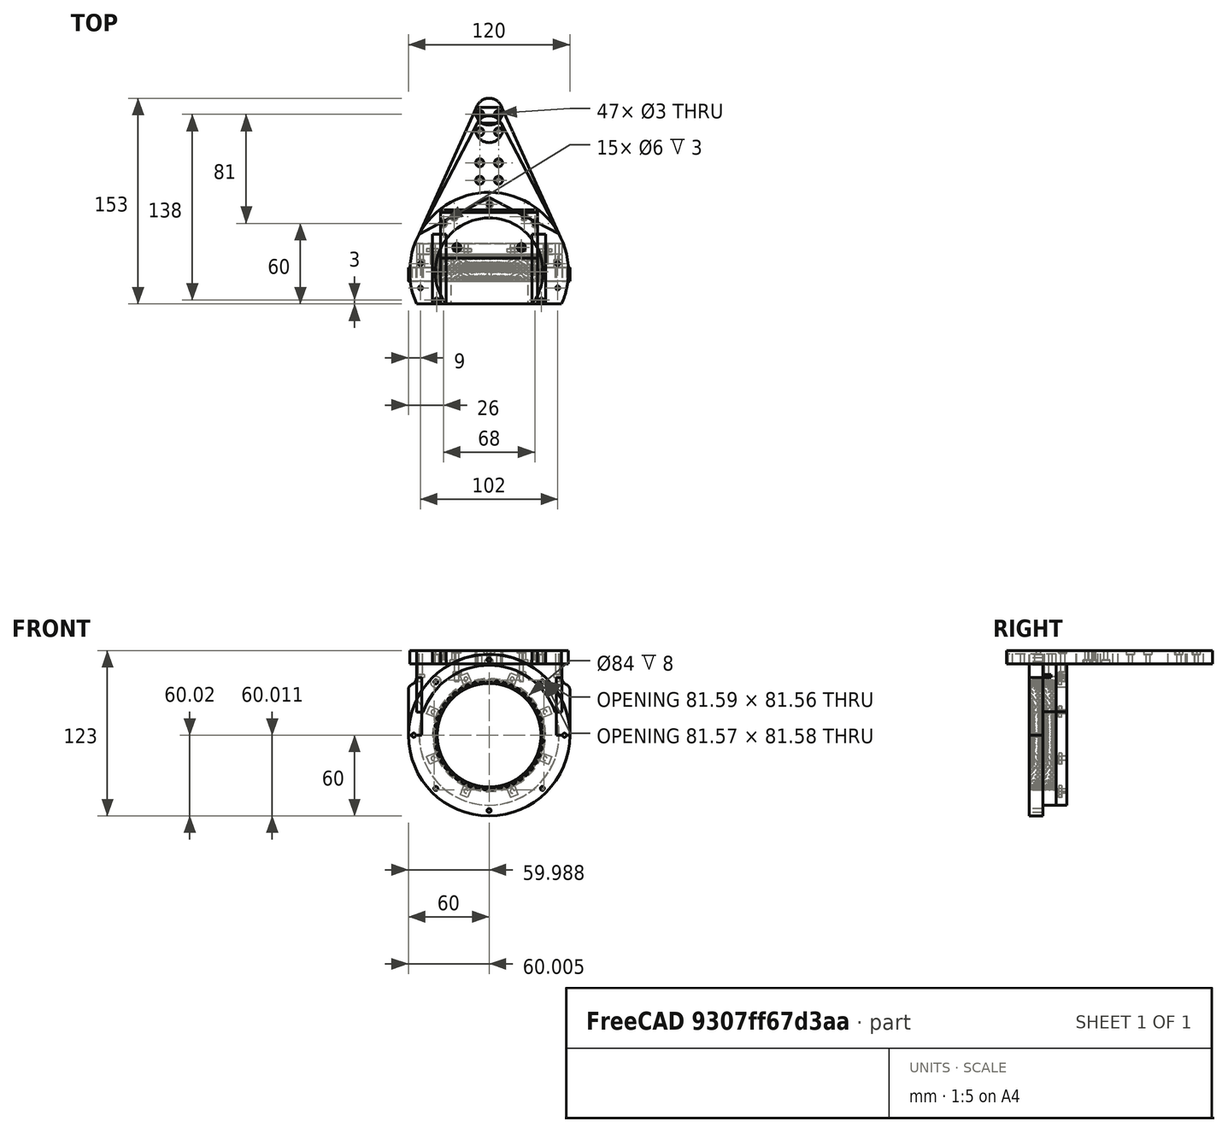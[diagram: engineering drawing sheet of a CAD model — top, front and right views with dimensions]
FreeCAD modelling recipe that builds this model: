
FCSTD DOCUMENT  (FreeCAD 0.19R24276 (Git))
Label: bazovina-part-A_trojuhelnikovina_012
License: All rights reserved
LicenseURL: http://en.wikipedia.org/wiki/All_rights_reserved
objects: Part::Cylinder×172, Part::Compound×74, Part::Cut×62, Part::Box×39, Part::FeaturePython×5, Part::Fillet×3, Sketcher::SketchObject×2, PartDesign::Pad×2, PartDesign::Body×2, Mesh::Feature×1
note: 363 computed .brp shape members not serialized (recipe doc carries the construction recipe); baked Part::Feature solids carry a one-line shape summary decoded from their .brp

FEATURE [Part::Cylinder] Cylinder284  label="Válec284"
  Angle = 360
  AttacherType = Attacher::AttachEngine3D
  Height = 10
  Placement = pos=(0,106,0) rot=(0,0,1;0rad)
  Radius = 10
FEATURE [Part::Box] Box135  label="Krychle135"
  AttacherType = Attacher::AttachEngine3D
  Height = 32
  Length = 200
  Placement = pos=(-100,-124,0) rot=(0,0,1;0rad)
  Width = 100
FEATURE [Part::Box] Box136  label="Krychle136"
  AttacherType = Attacher::AttachEngine3D
  Height = 10
  Length = 10
  Placement = pos=(32,-24,0) rot=(0,0,1;0rad)
  Width = 52
FEATURE [Part::FeaturePython] Tube  # WARN: FeaturePython — macro-defined, semantics opaque (R4)
  AttacherType = Attacher::AttachEngine3D
  Height = 10
  InnerRadius = 40
  OuterRadius = 59
FEATURE [Part::Cylinder] Cylinder292  label="Válec292"
  Angle = 360
  AttacherType = Attacher::AttachEngine3D
  Height = 100
  Placement = pos=(51,-12,0) rot=(0,0,1;0rad)
  Radius = 1.5
FEATURE [Part::Cylinder] Cylinder312  label="Válec312"
  Angle = 360
  AttacherType = Attacher::AttachEngine3D
  Height = 4
  Placement = pos=(34,36,-1) rot=(0,0,1;0rad)
  Radius = 3
FEATURE [Part::Cylinder] Cylinder311  label="Válec311"
  Angle = 360
  AttacherType = Attacher::AttachEngine3D
  Height = 4
  Placement = pos=(-34,36,-1) rot=(0,0,1;0rad)
  Radius = 3
FEATURE [Part::Compound] Compound290
  Links = -> [Cylinder312,Cylinder311]
FEATURE [Part::Cut] Cut136
  Base = -> Tube
  Tool = -> Compound290
FEATURE [Part::Box] Box137  label="Krychle137"
  AttacherType = Attacher::AttachEngine3D
  Height = 10
  Length = 10
  Placement = pos=(-42,-24,0) rot=(0,0,1;0rad)
  Width = 52
FEATURE [Part::Box] Box138  label="Krychle138"
  AttacherType = Attacher::AttachEngine3D
  Height = 10
  Length = 72
  Placement = pos=(-36,10,0) rot=(0,0,1;0rad)
  Width = 34
FEATURE [Part::Cylinder] Cylinder291  label="Válec291"
  Angle = 360
  AttacherType = Attacher::AttachEngine3D
  Height = 100
  Placement = pos=(-51,-12,0) rot=(0,0,1;0rad)
  Radius = 1.5
FEATURE [Part::Compound] Compound292
  Links = -> [Cylinder291,Cylinder292]
FEATURE [Part::Cylinder] Cylinder324  label="Válec324"
  Angle = 360
  AttacherType = Attacher::AttachEngine3D
  Height = 4
  Placement = pos=(51,7,0) rot=(0,0,1;0rad)
  Radius = 3
FEATURE [Part::Cylinder] Cylinder325  label="Válec325"
  Angle = 360
  AttacherType = Attacher::AttachEngine3D
  Height = 4
  Placement = pos=(-24,18,0) rot=(0,0,1;0rad)
  Radius = 3
FEATURE [Part::Cylinder] Cylinder326  label="Válec326"
  Angle = 360
  AttacherType = Attacher::AttachEngine3D
  Height = 4
  Placement = pos=(24,18,0) rot=(0,0,1;0rad)
  Radius = 3
FEATURE [Part::Cylinder] Cylinder315  label="Válec315"
  Angle = 360
  AttacherType = Attacher::AttachEngine3D
  Height = 4
  Placement = pos=(-51,-16,0) rot=(0,0,1;0rad)
  Radius = 3
FEATURE [Part::Cylinder] Cylinder314  label="Válec314"
  Angle = 360
  AttacherType = Attacher::AttachEngine3D
  Height = 50
  Placement = pos=(-34,36,0) rot=(0,0,1;0rad)
  Radius = 1.5
FEATURE [Part::Cylinder] Cylinder328  label="Válec328"
  Angle = 360
  AttacherType = Attacher::AttachEngine3D
  Height = 50
  Placement = pos=(-51,6,0) rot=(0,0,1;0rad)
  Radius = 1.5
FEATURE [Part::Cylinder] Cylinder327  label="Válec327"
  Angle = 360
  AttacherType = Attacher::AttachEngine3D
  Height = 4
  Placement = pos=(-24,18,0) rot=(0,0,1;0rad)
  Radius = 3
FEATURE [Part::Cylinder] Cylinder319  label="Válec319"
  Angle = 360
  AttacherType = Attacher::AttachEngine3D
  Height = 50
  Placement = pos=(51,6,0) rot=(0,0,1;0rad)
  Radius = 1.5
FEATURE [Part::Cylinder] Cylinder313  label="Válec313"
  Angle = 360
  AttacherType = Attacher::AttachEngine3D
  Height = 50
  Placement = pos=(34,36,0) rot=(0,0,1;0rad)
  Radius = 1.5
FEATURE [Part::Compound] Compound291
  Links = -> [Cylinder314,Cylinder313]
FEATURE [Part::Cylinder] Cylinder323  label="Válec323"
  Angle = 360
  AttacherType = Attacher::AttachEngine3D
  Height = 4
  Placement = pos=(-51,7,0) rot=(0,0,1;0rad)
  Radius = 3
FEATURE [Part::Compound] Compound296
  Links = -> [Cylinder324,Cylinder323,Cylinder325,Cylinder326]
  Placement = pos=(0,0,8) rot=(0,0,1;0rad)
FEATURE [Part::Cylinder] Cylinder329  label="Válec329"
  Angle = 360
  AttacherType = Attacher::AttachEngine3D
  Height = 50
  Placement = pos=(51,6,0) rot=(0,0,1;0rad)
  Radius = 1.5
FEATURE [Part::Cylinder] Cylinder330  label="Válec330"
  Angle = 360
  AttacherType = Attacher::AttachEngine3D
  Height = 50
  Placement = pos=(-24,18,0) rot=(0,0,1;0rad)
  Radius = 1.5
FEATURE [Part::Cylinder] Cylinder316  label="Válec316"
  Angle = 360
  AttacherType = Attacher::AttachEngine3D
  Height = 4
  Placement = pos=(51,-16,0) rot=(0,0,1;0rad)
  Radius = 3
FEATURE [Part::Compound] Compound293
  Links = -> [Cylinder315,Cylinder316]
  Placement = pos=(0,0,25) rot=(0,0,1;0rad)
FEATURE [Part::Cylinder] Cylinder320  label="Válec320"
  Angle = 360
  AttacherType = Attacher::AttachEngine3D
  Height = 50
  Placement = pos=(-51,6,0) rot=(0,0,1;0rad)
  Radius = 1.5
FEATURE [Part::Cylinder] Cylinder321  label="Válec321"
  Angle = 360
  AttacherType = Attacher::AttachEngine3D
  Height = 50
  Placement = pos=(-24,18,0) rot=(0,0,1;0rad)
  Radius = 1.5
FEATURE [Part::Cylinder] Cylinder322  label="Válec322"
  Angle = 360
  AttacherType = Attacher::AttachEngine3D
  Height = 50
  Placement = pos=(24,18,0) rot=(0,0,1;0rad)
  Radius = 1.5
FEATURE [Part::Compound] Compound295
  Links = -> [Cylinder319,Cylinder320,Cylinder321,Cylinder322]
FEATURE [Part::Cut] Cut137
  Base = -> Cut136
  Tool = -> Compound291
FEATURE [Part::Cut] Cut138
  Base = -> Cut137
  Tool = -> Compound293
FEATURE [Part::Cut] Cut139
  Base = -> Cut138
  Tool = -> Compound292
FEATURE [Part::Cylinder] Cylinder334  label="Válec334"
  Angle = 360
  AttacherType = Attacher::AttachEngine3D
  Height = 4
  Placement = pos=(24,18,0) rot=(0,0,1;0rad)
  Radius = 3
FEATURE [Part::Compound] Compound298
  Links = -> [Cylinder327,Cylinder334]
  Placement = pos=(0,0,7) rot=(0,0,1;0rad)
FEATURE [Part::Cut] Cut142
  Base = -> Cut139
  Tool = -> Compound298
FEATURE [Part::Cylinder] Cylinder331  label="Válec331"
  Angle = 360
  AttacherType = Attacher::AttachEngine3D
  Height = 50
  Placement = pos=(24,18,0) rot=(0,0,1;0rad)
  Radius = 1.5
FEATURE [Part::Compound] Compound297
  Links = -> [Cylinder329,Cylinder328,Cylinder330,Cylinder331]
FEATURE [Part::Cut] Cut143
  Base = -> Cut142
  Tool = -> Compound297
FEATURE [Part::Cut] Cut144
  Base = -> Cut143
  Tool = -> Box135
FEATURE [Part::Cylinder] Cylinder297  label="Válec297"
  Angle = 360
  AttacherType = Attacher::AttachEngine3D
  Height = 4
  Placement = pos=(34,36,-1) rot=(0,0,1;0rad)
  Radius = 3
FEATURE [Part::Cylinder] Cylinder363  label="Válec363"
  Angle = 360
  AttacherType = Attacher::AttachEngine3D
  Height = 4
  Placement = pos=(0,50,-1) rot=(0,0,1;0rad)
  Radius = 3
FEATURE [Part::Cut] Cut153
  Base = -> Cut144
  Tool = -> Cylinder363
FEATURE [Part::Cylinder] Cylinder364  label="Válec364"
  Angle = 360
  AttacherType = Attacher::AttachEngine3D
  Height = 50
  Placement = pos=(0,50,0) rot=(0,0,1;0rad)
  Radius = 1.5
FEATURE [Part::Cut] Cut154
  Base = -> Cut153
  Tool = -> Cylinder364
FEATURE [Part::Cylinder] Cylinder298  label="Válec298"
  Angle = 360
  AttacherType = Attacher::AttachEngine3D
  Height = 4
  Placement = pos=(-34,36,-1) rot=(0,0,1;0rad)
  Radius = 3
FEATURE [Part::Compound] Compound282
  Links = -> [Cylinder298,Cylinder297]
FEATURE [Part::Cut] Cut131
  Base = -> Box138
  Tool = -> Compound282
FEATURE [Part::Cylinder] Cylinder294  label="Válec294"
  Angle = 360
  AttacherType = Attacher::AttachEngine3D
  Height = 50
  Placement = pos=(-34,36,0) rot=(0,0,1;0rad)
  Radius = 1.5
FEATURE [Part::Cylinder] Cylinder293  label="Válec293"
  Angle = 360
  AttacherType = Attacher::AttachEngine3D
  Height = 50
  Placement = pos=(34,36,0) rot=(0,0,1;0rad)
  Radius = 1.5
FEATURE [Part::Compound] Compound284
  Links = -> [Cylinder294,Cylinder293]
FEATURE [Part::Cut] Cut132
  Base = -> Cut131
  Tool = -> Compound284
FEATURE [Part::Cut] Cut140
  Base = -> Cut132
  Tool = -> Compound296
FEATURE [Part::Cut] Cut141
  Base = -> Cut140
  Tool = -> Compound295
FEATURE [Part::Cylinder] Cylinder424  label="Válec424"
  Angle = 360
  AttacherType = Attacher::AttachEngine3D
  Height = 4
  Placement = pos=(-7,-34,73) rot=(1,0,0;1.5708rad)
  Radius = 3
FEATURE [Part::Cylinder] Cylinder413  label="Válec413"
  Angle = 360
  AttacherType = Attacher::AttachEngine3D
  Height = 20
  Placement = pos=(7,-34,37) rot=(1,0,0;1.5708rad)
  Radius = 1.5
FEATURE [Part::Cylinder] Cylinder414  label="Válec414"
  Angle = 360
  AttacherType = Attacher::AttachEngine3D
  Height = 20
  Placement = pos=(7,-34,73) rot=(1,0,0;1.5708rad)
  Radius = 1.5
FEATURE [Part::Cylinder] Cylinder415  label="Válec415"
  Angle = 360
  AttacherType = Attacher::AttachEngine3D
  Height = 20
  Placement = pos=(-7,-34,37) rot=(1,0,0;1.5708rad)
  Radius = 1.5
FEATURE [Part::Cylinder] Cylinder412  label="Válec412"
  Angle = 360
  AttacherType = Attacher::AttachEngine3D
  Height = 20
  Placement = pos=(-7,-34,73) rot=(1,0,0;1.5708rad)
  Radius = 1.5
FEATURE [Part::Compound] Compound317
  Links = -> [Cylinder413,Cylinder415,Cylinder414,Cylinder412]
  Placement = pos=(0,141,45) rot=(1,0,0;1.5708rad)
FEATURE [Part::Cut] Cut166
  Base = -> Cylinder284
  Tool = -> Compound317
FEATURE [Part::Cylinder] Cylinder427  label="Válec427"
  Angle = 360
  AttacherType = Attacher::AttachEngine3D
  Height = 4
  Placement = pos=(-7,-34,37) rot=(1,0,0;1.5708rad)
  Radius = 3
FEATURE [Part::Cylinder] Cylinder426  label="Válec426"
  Angle = 360
  AttacherType = Attacher::AttachEngine3D
  Height = 4
  Placement = pos=(7,-34,73) rot=(1,0,0;1.5708rad)
  Radius = 3
FEATURE [Part::Cylinder] Cylinder425  label="Válec425"
  Angle = 360
  AttacherType = Attacher::AttachEngine3D
  Height = 4
  Placement = pos=(7,-34,37) rot=(1,0,0;1.5708rad)
  Radius = 3
FEATURE [Part::Compound] Compound320
  Links = -> [Cylinder425,Cylinder427,Cylinder426,Cylinder424]
  Placement = pos=(0,141,45) rot=(1,0,0;1.5708rad)
FEATURE [Part::Cut] Cut168
  Base = -> Cut166
  Tool = -> Compound320
FEATURE [Sketcher::SketchObject] Sketch
  FullyConstrained = false
  MapMode = 5
  Support = -> [XY_Plane]
  sketch-geometry (5):
    g0: LineSegment StartX=-51.8839 StartY=28.0157 StartZ=0 EndX=-8.82571 EndY=110.528 EndZ=0
    g1: LineSegment StartX=-8.82571 StartY=110.528 StartZ=0 EndX=8.88346 EndY=110.528 EndZ=0
    g2: LineSegment StartX=8.88346 StartY=110.528 StartZ=0 EndX=51.7746 EndY=28.1985 EndZ=0
    g3: LineSegment StartX=51.7746 StartY=28.1985 StartZ=0 EndX=0 EndY=55.1408 EndZ=0
    g4: LineSegment StartX=0 StartY=55.1408 StartZ=0 EndX=-51.8839 EndY=28.0157 EndZ=0
  constraints (7):
    c: Coincident(g0,g1)
    c: Horizontal(g1)
    c: Coincident(g1,g2)
    c: Coincident(g2,g3)
    c: PointOnObject(g3,g-2)
    c: Coincident(g3,g4)
    c: Coincident(g4,g0)
FEATURE [PartDesign::Pad] Pad
  Direction = (1,1,1)
  Length = 10
  Length2 = 100
  Profile = -> Sketch
  Type = 0
FEATURE [PartDesign::Body] Body
  Group = -> [Sketch,Pad]
  Origin = -> Origin
  Tip = -> Pad
FEATURE [Part::Cylinder] Cylinder307  label="Válec307"
  Angle = 360
  AttacherType = Attacher::AttachEngine3D
  Height = 4
  Placement = pos=(-34,36,-1) rot=(0,0,1;0rad)
  Radius = 3
FEATURE [Part::Cylinder] Cylinder308  label="Válec308"
  Angle = 360
  AttacherType = Attacher::AttachEngine3D
  Height = 4
  Placement = pos=(34,36,-1) rot=(0,0,1;0rad)
  Radius = 3
FEATURE [Part::Compound] Compound288
  Links = -> [Cylinder308,Cylinder307]
FEATURE [Part::Cut] Cut134
  Base = -> Body
  Tool = -> Compound288
FEATURE [Part::Cylinder] Cylinder309  label="Válec309"
  Angle = 360
  AttacherType = Attacher::AttachEngine3D
  Height = 50
  Placement = pos=(34,36,0) rot=(0,0,1;0rad)
  Radius = 1.5
FEATURE [Part::Cylinder] Cylinder310  label="Válec310"
  Angle = 360
  AttacherType = Attacher::AttachEngine3D
  Height = 50
  Placement = pos=(-34,36,0) rot=(0,0,1;0rad)
  Radius = 1.5
FEATURE [Part::Compound] Compound289
  Links = -> [Cylinder310,Cylinder309]
FEATURE [Part::Cut] Cut135
  Base = -> Cut134
  Tool = -> Compound289
FEATURE [Part::Cylinder] Cylinder421  label="Válec421"
  Angle = 360
  AttacherType = Attacher::AttachEngine3D
  Height = 4
  Placement = pos=(7,-34,37) rot=(1,0,0;1.5708rad)
  Radius = 3
FEATURE [Part::Cylinder] Cylinder419  label="Válec419"
  Angle = 360
  AttacherType = Attacher::AttachEngine3D
  Height = 20
  Placement = pos=(-7,-34,37) rot=(1,0,0;1.5708rad)
  Radius = 1.5
FEATURE [Part::Cylinder] Cylinder417  label="Válec417"
  Angle = 360
  AttacherType = Attacher::AttachEngine3D
  Height = 20
  Placement = pos=(7,-34,37) rot=(1,0,0;1.5708rad)
  Radius = 1.5
FEATURE [Part::Cylinder] Cylinder418  label="Válec418"
  Angle = 360
  AttacherType = Attacher::AttachEngine3D
  Height = 20
  Placement = pos=(7,-34,73) rot=(1,0,0;1.5708rad)
  Radius = 1.5
FEATURE [Part::Cylinder] Cylinder416  label="Válec416"
  Angle = 360
  AttacherType = Attacher::AttachEngine3D
  Height = 20
  Placement = pos=(-7,-34,73) rot=(1,0,0;1.5708rad)
  Radius = 1.5
FEATURE [Part::Compound] Compound318
  Links = -> [Cylinder417,Cylinder419,Cylinder418,Cylinder416]
  Placement = pos=(0,141,45) rot=(1,0,0;1.5708rad)
FEATURE [Part::Cut] Cut165
  Base = -> Cut135
  Tool = -> Compound318
FEATURE [Part::Cylinder] Cylinder420  label="Válec420"
  Angle = 360
  AttacherType = Attacher::AttachEngine3D
  Height = 4
  Placement = pos=(-7,-34,73) rot=(1,0,0;1.5708rad)
  Radius = 3
FEATURE [Part::Cylinder] Cylinder423  label="Válec423"
  Angle = 360
  AttacherType = Attacher::AttachEngine3D
  Height = 4
  Placement = pos=(-7,-34,37) rot=(1,0,0;1.5708rad)
  Radius = 3
FEATURE [Part::Cylinder] Cylinder422  label="Válec422"
  Angle = 360
  AttacherType = Attacher::AttachEngine3D
  Height = 4
  Placement = pos=(7,-34,73) rot=(1,0,0;1.5708rad)
  Radius = 3
FEATURE [Part::Compound] Compound319
  Links = -> [Cylinder421,Cylinder423,Cylinder422,Cylinder420]
  Placement = pos=(0,141,45) rot=(1,0,0;1.5708rad)
FEATURE [Part::Cut] Cut167
  Base = -> Cut165
  Tool = -> Compound319
FEATURE [Part::Cylinder] Cylinder531  label="Válec531"
  Angle = 360
  AttacherType = Attacher::AttachEngine3D
  Height = 100
  Placement = pos=(39,-21,0) rot=(0,0,1;0rad)
  Radius = 1.5
FEATURE [Part::Cylinder] Cylinder530  label="Válec530"
  Angle = 360
  AttacherType = Attacher::AttachEngine3D
  Height = 100
  Placement = pos=(-39,-21,0) rot=(0,0,1;0rad)
  Radius = 1.5
FEATURE [Part::Compound] Compound308
  Links = -> [Cylinder530,Cylinder531]
FEATURE [Part::Cylinder] Cylinder532  label="Válec532"
  Angle = 360
  AttacherType = Attacher::AttachEngine3D
  Height = 100
  Placement = pos=(-39,-21,0) rot=(0,0,1;0rad)
  Radius = 1.5
FEATURE [Part::Cylinder] Cylinder533  label="Válec533"
  Angle = 360
  AttacherType = Attacher::AttachEngine3D
  Height = 100
  Placement = pos=(39,-21,0) rot=(0,0,1;0rad)
  Radius = 1.5
FEATURE [Part::Compound] Compound321
  Links = -> [Cylinder532,Cylinder533]
FEATURE [Part::Compound] Compound
  Links = -> [Box136,Box137]
FEATURE [Part::Cut] Cut
  Base = -> Compound
  Tool = -> Compound321
FEATURE [Part::Cut] Cut169
  Base = -> Cut154
  Tool = -> Compound308
FEATURE [Part::Compound] Compound322  label="bazovina_part-A_trojuhelnikovina"
  Links = -> [Cut141,Cut168,Cut167,Cut,Cut169]
FEATURE [Sketcher::SketchObject] Sketch001
  FullyConstrained = false
  MapMode = 5
  Support = -> [XY_Plane001]
  sketch-geometry (5):
    g0: LineSegment StartX=-51.8839 StartY=28.0157 StartZ=0 EndX=-9.41248 EndY=122.349 EndZ=0
    g1: LineSegment StartX=-9.41248 StartY=122.349 StartZ=0 EndX=9.41746 EndY=122.349 EndZ=0
    g2: LineSegment StartX=9.41746 StartY=122.349 StartZ=0 EndX=51.7746 EndY=28.1985 EndZ=0
    g3: LineSegment StartX=51.7746 StartY=28.1985 StartZ=0 EndX=0 EndY=55.1408 EndZ=0
    g4: LineSegment StartX=0 StartY=55.1408 StartZ=0 EndX=-51.8839 EndY=28.0157 EndZ=0
  constraints (7):
    c: Coincident(g0,g1)
    c: Horizontal(g1)
    c: Coincident(g1,g2)
    c: Coincident(g2,g3)
    c: PointOnObject(g3,g-2)
    c: Coincident(g3,g4)
    c: Coincident(g4,g0)
FEATURE [Part::Cylinder] Cylinder534  label="Válec534"
  Angle = 360
  AttacherType = Attacher::AttachEngine3D
  Height = 10
  Placement = pos=(0,106,0) rot=(0,0,1;0rad)
  Radius = 10
FEATURE [Part::Box] Box139  label="Krychle139"
  AttacherType = Attacher::AttachEngine3D
  Height = 32
  Length = 200
  Placement = pos=(-100,-124,0) rot=(0,0,1;0rad)
  Width = 100
FEATURE [Part::Box] Box140  label="Krychle140"
  AttacherType = Attacher::AttachEngine3D
  Height = 10
  Length = 10
  Placement = pos=(32,-24,0) rot=(0,0,1;0rad)
  Width = 52
FEATURE [Part::Cylinder] Cylinder535  label="Válec535"
  Angle = 360
  AttacherType = Attacher::AttachEngine3D
  Height = 100
  Placement = pos=(51,-12,0) rot=(0,0,1;0rad)
  Radius = 1.5
FEATURE [Part::Box] Box141  label="Krychle141"
  AttacherType = Attacher::AttachEngine3D
  Height = 10
  Length = 10
  Placement = pos=(-42,-24,0) rot=(0,0,1;0rad)
  Width = 52
FEATURE [Part::Box] Box142  label="Krychle142"
  AttacherType = Attacher::AttachEngine3D
  Height = 10
  Length = 72
  Placement = pos=(-36,-24,0) rot=(0,0,1;0rad)
  Width = 70
FEATURE [Part::Cylinder] Cylinder538  label="Válec538"
  Angle = 360
  AttacherType = Attacher::AttachEngine3D
  Height = 100
  Placement = pos=(-51,-12,0) rot=(0,0,1;0rad)
  Radius = 1.5
FEATURE [Part::Compound] Compound323
  Links = -> [Cylinder538,Cylinder535]
FEATURE [PartDesign::Pad] Pad001
  Direction = (1,1,1)
  Length = 10
  Length2 = 100
  Profile = -> Sketch001
  Type = 0
FEATURE [Part::FeaturePython] Tube001  # WARN: FeaturePython — macro-defined, semantics opaque (R4)
  AttacherType = Attacher::AttachEngine3D
  Height = 10
  InnerRadius = 40
  OuterRadius = 59
FEATURE [PartDesign::Body] Body001
  Group = -> [Sketch001,Pad001]
  Origin = -> Origin001
  Tip = -> Pad001
FEATURE [Part::Cylinder] Cylinder544  label="Válec544"
  Angle = 360
  AttacherType = Attacher::AttachEngine3D
  Height = 50
  Placement = pos=(-51,6,0) rot=(0,0,1;0rad)
  Radius = 1.5
FEATURE [Part::Cylinder] Cylinder549  label="Válec549"
  Angle = 360
  AttacherType = Attacher::AttachEngine3D
  Height = 50
  Placement = pos=(51,6,0) rot=(0,0,1;0rad)
  Radius = 1.5
FEATURE [Part::Cylinder] Cylinder550  label="Válec550"
  Angle = 360
  AttacherType = Attacher::AttachEngine3D
  Height = 50
  Placement = pos=(-24,18,0) rot=(0,0,1;0rad)
  Radius = 1.5
FEATURE [Part::Cylinder] Cylinder556  label="Válec556"
  Angle = 360
  AttacherType = Attacher::AttachEngine3D
  Height = 50
  Placement = pos=(24,18,0) rot=(0,0,1;0rad)
  Radius = 1.5
FEATURE [Part::Compound] Compound324
  Links = -> [Cylinder549,Cylinder544,Cylinder550,Cylinder556]
FEATURE [Part::Cylinder] Cylinder563  label="Válec563"
  Angle = 360
  AttacherType = Attacher::AttachEngine3D
  Height = 4
  Placement = pos=(-7,-34,73) rot=(1,0,0;1.5708rad)
  Radius = 3
FEATURE [Part::Cylinder] Cylinder564  label="Válec564"
  Angle = 360
  AttacherType = Attacher::AttachEngine3D
  Height = 20
  Placement = pos=(7,-34,37) rot=(1,0,0;1.5708rad)
  Radius = 1.5
FEATURE [Part::Cylinder] Cylinder565  label="Válec565"
  Angle = 360
  AttacherType = Attacher::AttachEngine3D
  Height = 20
  Placement = pos=(7,-34,73) rot=(1,0,0;1.5708rad)
  Radius = 1.5
FEATURE [Part::Cylinder] Cylinder566  label="Válec566"
  Angle = 360
  AttacherType = Attacher::AttachEngine3D
  Height = 20
  Placement = pos=(-7,-34,37) rot=(1,0,0;1.5708rad)
  Radius = 1.5
FEATURE [Part::Cylinder] Cylinder567  label="Válec567"
  Angle = 360
  AttacherType = Attacher::AttachEngine3D
  Height = 20
  Placement = pos=(-7,-34,73) rot=(1,0,0;1.5708rad)
  Radius = 1.5
FEATURE [Part::Compound] Compound333
  Links = -> [Cylinder564,Cylinder566,Cylinder565,Cylinder567]
  Placement = pos=(0,141,45) rot=(1,0,0;1.5708rad)
FEATURE [Part::Cut] Cut189
  Base = -> Cylinder534
  Tool = -> Compound333
FEATURE [Part::Cylinder] Cylinder568  label="Válec568"
  Angle = 360
  AttacherType = Attacher::AttachEngine3D
  Height = 4
  Placement = pos=(-7,-34,37) rot=(1,0,0;1.5708rad)
  Radius = 3
FEATURE [Part::Cylinder] Cylinder569  label="Válec569"
  Angle = 360
  AttacherType = Attacher::AttachEngine3D
  Height = 4
  Placement = pos=(7,-34,73) rot=(1,0,0;1.5708rad)
  Radius = 3
FEATURE [Part::Cylinder] Cylinder570  label="Válec570"
  Angle = 360
  AttacherType = Attacher::AttachEngine3D
  Height = 4
  Placement = pos=(7,-34,37) rot=(1,0,0;1.5708rad)
  Radius = 3
FEATURE [Part::Compound] Compound332
  Links = -> [Cylinder570,Cylinder568,Cylinder569,Cylinder563]
  Placement = pos=(0,141,45) rot=(1,0,0;1.5708rad)
FEATURE [Part::Cut] Cut190
  Base = -> Cut189
  Placement = pos=(0,13,0) rot=(0,0,1;0rad)
  Tool = -> Compound332
FEATURE [Part::Cylinder] Cylinder575  label="Válec575"
  Angle = 360
  AttacherType = Attacher::AttachEngine3D
  Height = 4
  Placement = pos=(7,-34,37) rot=(1,0,0;1.5708rad)
  Radius = 3
FEATURE [Part::Cylinder] Cylinder576  label="Válec576"
  Angle = 360
  AttacherType = Attacher::AttachEngine3D
  Height = 20
  Placement = pos=(-7,-34,37) rot=(1,0,0;1.5708rad)
  Radius = 1.5
FEATURE [Part::Compound] Compound341
  Links = -> [Box140,Box141]
FEATURE [Part::Cylinder] Cylinder577  label="Válec577"
  Angle = 360
  AttacherType = Attacher::AttachEngine3D
  Height = 20
  Placement = pos=(7,-34,37) rot=(1,0,0;1.5708rad)
  Radius = 1.5
FEATURE [Part::Cylinder] Cylinder578  label="Válec578"
  Angle = 360
  AttacherType = Attacher::AttachEngine3D
  Height = 20
  Placement = pos=(7,-34,73) rot=(1,0,0;1.5708rad)
  Radius = 1.5
FEATURE [Part::Cylinder] Cylinder579  label="Válec579"
  Angle = 360
  AttacherType = Attacher::AttachEngine3D
  Height = 20
  Placement = pos=(-7,-34,73) rot=(1,0,0;1.5708rad)
  Radius = 1.5
FEATURE [Part::Compound] Compound337
  Links = -> [Cylinder577,Cylinder576,Cylinder578,Cylinder579]
  Placement = pos=(0,154,45) rot=(1,0,0;1.5708rad)
FEATURE [Part::Cylinder] Cylinder580  label="Válec580"
  Angle = 360
  AttacherType = Attacher::AttachEngine3D
  Height = 4
  Placement = pos=(-7,-34,73) rot=(1,0,0;1.5708rad)
  Radius = 3
FEATURE [Part::Cylinder] Cylinder581  label="Válec581"
  Angle = 360
  AttacherType = Attacher::AttachEngine3D
  Height = 4
  Placement = pos=(-7,-34,37) rot=(1,0,0;1.5708rad)
  Radius = 3
FEATURE [Part::Cylinder] Cylinder582  label="Válec582"
  Angle = 360
  AttacherType = Attacher::AttachEngine3D
  Height = 4
  Placement = pos=(7,-34,73) rot=(1,0,0;1.5708rad)
  Radius = 3
FEATURE [Part::Compound] Compound338
  Links = -> [Cylinder575,Cylinder581,Cylinder582,Cylinder580]
  Placement = pos=(0,154,45) rot=(1,0,0;1.5708rad)
FEATURE [Part::Cylinder] Cylinder583  label="Válec583"
  Angle = 360
  AttacherType = Attacher::AttachEngine3D
  Height = 100
  Placement = pos=(39,-21,0) rot=(0,0,1;0rad)
  Radius = 1.5
FEATURE [Part::Cylinder] Cylinder584  label="Válec584"
  Angle = 360
  AttacherType = Attacher::AttachEngine3D
  Height = 100
  Placement = pos=(-39,-21,0) rot=(0,0,1;0rad)
  Radius = 1.5
FEATURE [Part::Compound] Compound339
  Links = -> [Cylinder584,Cylinder583]
FEATURE [Part::Cylinder] Cylinder585  label="Válec585"
  Angle = 360
  AttacherType = Attacher::AttachEngine3D
  Height = 100
  Placement = pos=(-39,-21,0) rot=(0,0,1;0rad)
  Radius = 1.5
FEATURE [Part::Cylinder] Cylinder586  label="Válec586"
  Angle = 360
  AttacherType = Attacher::AttachEngine3D
  Height = 100
  Placement = pos=(39,-21,0) rot=(0,0,1;0rad)
  Radius = 1.5
FEATURE [Part::Compound] Compound340
  Links = -> [Cylinder585,Cylinder586]
FEATURE [Part::Cut] Cut173
  Base = -> Compound341
  Tool = -> Compound340
FEATURE [Part::Box] Box236  label="Krychle236"
  AttacherType = Attacher::AttachEngine3D
  Height = 64
  Length = 6
  Placement = pos=(11,-3,-93) rot=(0,0,1;0rad)
  Width = 6
FEATURE [Part::Box] Box237  label="Krychle237"
  AttacherType = Attacher::AttachEngine3D
  Height = 64
  Length = 6
  Placement = pos=(87,-3,-93) rot=(0,0,1;0rad)
  Width = 6
FEATURE [Part::Compound] Compound627
  Links = -> [Box236,Box237]
  Placement = pos=(-52,0,36) rot=(0,0,1;0rad)
FEATURE [Part::Cylinder] Cylinder1238  label="Válec1238"
  Angle = 360
  AttacherType = Attacher::AttachEngine3D
  Height = 100
  Placement = pos=(90,0,-60) rot=(0,0,1;0rad)
  Radius = 1.5
FEATURE [Part::Cylinder] Cylinder1239  label="Válec1239"
  Angle = 360
  AttacherType = Attacher::AttachEngine3D
  Height = 100
  Placement = pos=(14,0,-60) rot=(0,0,1;0rad)
  Radius = 1.5
FEATURE [Part::Compound] Compound625  label="srouby_troj001"
  Links = -> [Cylinder1238,Cylinder1239]
  Placement = pos=(-52,0,0) rot=(0,0,1;0rad)
FEATURE [Part::Cylinder] Cylinder1232  label="Válec1232"
  Angle = 360
  AttacherType = Attacher::AttachEngine3D
  Height = 32
  Placement = pos=(26,41,-42) rot=(0,0,1;0rad)
  Radius = 1.5
FEATURE [Part::Cylinder] Cylinder1233  label="Válec1233"
  Angle = 360
  AttacherType = Attacher::AttachEngine3D
  Height = 32
  Placement = pos=(78,41,-42) rot=(0,0,1;0rad)
  Radius = 1.5
FEATURE [Part::Compound] Compound620
  Links = -> [Cylinder1232,Cylinder1233]
  Placement = pos=(-52,0,36) rot=(0,0,1;0rad)
FEATURE [Part::Cut] Cut191
  Base = -> Tube001
  Tool = -> Box139
FEATURE [Part::Compound] Compound628
  Links = -> [Compound339,Compound324,Compound323]
  Placement = pos=(0,0,-10) rot=(0,0,1;0rad)
FEATURE [Part::Compound] Compound630
  Links = -> [Compound625,Compound620]
FEATURE [Part::Cylinder] Cylinder1242  label="Válec1242"
  Angle = 360
  AttacherType = Attacher::AttachEngine3D
  Height = 3
  Placement = pos=(26,41,-42) rot=(0,0,1;0rad)
  Radius = 3
FEATURE [Part::Cylinder] Cylinder1243  label="Válec1243"
  Angle = 360
  AttacherType = Attacher::AttachEngine3D
  Height = 3
  Placement = pos=(78,41,-42) rot=(0,0,1;0rad)
  Radius = 3
FEATURE [Part::Compound] Compound633
  Links = -> [Cylinder1242,Cylinder1243]
  Placement = pos=(-52,0,42) rot=(0,0,1;0rad)
FEATURE [Part::Cylinder] Cylinder1244  label="Válec1244"
  Angle = 360
  AttacherType = Attacher::AttachEngine3D
  Height = 3
  Placement = pos=(26,41,-42) rot=(0,0,1;0rad)
  Radius = 3
FEATURE [Part::Cylinder] Cylinder1245  label="Válec1245"
  Angle = 360
  AttacherType = Attacher::AttachEngine3D
  Height = 3
  Placement = pos=(78,41,-42) rot=(0,0,1;0rad)
  Radius = 3
FEATURE [Part::Compound] Compound634
  Links = -> [Cylinder1244,Cylinder1245]
  Placement = pos=(-52,0,42) rot=(0,0,1;0rad)
FEATURE [Part::Cut] Cut192
  Base = -> Body001
  Tool = -> Compound337
FEATURE [Part::Cut] Cut193
  Base = -> Cut192
  Tool = -> Compound338
FEATURE [Part::Cylinder] Cylinder1246  label="Válec1246"
  Angle = 360
  AttacherType = Attacher::AttachEngine3D
  Height = 100
  Placement = pos=(51,-12,0) rot=(0,0,1;0rad)
  Radius = 1.5
FEATURE [Part::Cylinder] Cylinder1247  label="Válec1247"
  Angle = 360
  AttacherType = Attacher::AttachEngine3D
  Height = 100
  Placement = pos=(-51,-12,0) rot=(0,0,1;0rad)
  Radius = 1.5
FEATURE [Part::Compound] Compound636
  Links = -> [Cylinder1247,Cylinder1246]
FEATURE [Part::Cylinder] Cylinder1248  label="Válec1248"
  Angle = 360
  AttacherType = Attacher::AttachEngine3D
  Height = 50
  Placement = pos=(-51,6,0) rot=(0,0,1;0rad)
  Radius = 1.5
FEATURE [Part::Cylinder] Cylinder1249  label="Válec1249"
  Angle = 360
  AttacherType = Attacher::AttachEngine3D
  Height = 50
  Placement = pos=(51,6,0) rot=(0,0,1;0rad)
  Radius = 1.5
FEATURE [Part::Cylinder] Cylinder1250  label="Válec1250"
  Angle = 360
  AttacherType = Attacher::AttachEngine3D
  Height = 50
  Placement = pos=(-24,18,0) rot=(0,0,1;0rad)
  Radius = 1.5
FEATURE [Part::Cylinder] Cylinder1251  label="Válec1251"
  Angle = 360
  AttacherType = Attacher::AttachEngine3D
  Height = 50
  Placement = pos=(24,18,0) rot=(0,0,1;0rad)
  Radius = 1.5
FEATURE [Part::Compound] Compound637
  Links = -> [Cylinder1249,Cylinder1248,Cylinder1250,Cylinder1251]
FEATURE [Part::Cylinder] Cylinder1252  label="Válec1252"
  Angle = 360
  AttacherType = Attacher::AttachEngine3D
  Height = 100
  Placement = pos=(39,-21,0) rot=(0,0,1;0rad)
  Radius = 1.5
FEATURE [Part::Cylinder] Cylinder1253  label="Válec1253"
  Angle = 360
  AttacherType = Attacher::AttachEngine3D
  Height = 100
  Placement = pos=(-39,-21,0) rot=(0,0,1;0rad)
  Radius = 1.5
FEATURE [Part::Compound] Compound638
  Links = -> [Cylinder1253,Cylinder1252]
FEATURE [Part::Compound] Compound635
  Links = -> [Compound638,Compound637,Compound636]
  Placement = pos=(0,0,-10) rot=(0,0,1;0rad)
FEATURE [Part::Cut] Cut194
  Base = -> Cut191
  Tool = -> Compound635
FEATURE [Part::Cylinder] Cylinder1254  label="Válec1254"
  Angle = 360
  AttacherType = Attacher::AttachEngine3D
  Height = 100
  Placement = pos=(90,0,-60) rot=(0,0,1;0rad)
  Radius = 1.5
FEATURE [Part::Cylinder] Cylinder1255  label="Válec1255"
  Angle = 360
  AttacherType = Attacher::AttachEngine3D
  Height = 100
  Placement = pos=(14,0,-60) rot=(0,0,1;0rad)
  Radius = 1.5
FEATURE [Part::Compound] Compound640  label="srouby_troj002"
  Links = -> [Cylinder1254,Cylinder1255]
  Placement = pos=(-52,0,0) rot=(0,0,1;0rad)
FEATURE [Part::Cylinder] Cylinder1256  label="Válec1256"
  Angle = 360
  AttacherType = Attacher::AttachEngine3D
  Height = 32
  Placement = pos=(26,41,-42) rot=(0,0,1;0rad)
  Radius = 1.5
FEATURE [Part::Cylinder] Cylinder1257  label="Válec1257"
  Angle = 360
  AttacherType = Attacher::AttachEngine3D
  Height = 32
  Placement = pos=(78,41,-42) rot=(0,0,1;0rad)
  Radius = 1.5
FEATURE [Part::Compound] Compound641
  Links = -> [Cylinder1256,Cylinder1257]
  Placement = pos=(-52,0,36) rot=(0,0,1;0rad)
FEATURE [Part::Compound] Compound639
  Links = -> [Compound640,Compound641]
FEATURE [Part::Cut] Cut195
  Base = -> Cut194
  Tool = -> Compound639
FEATURE [Part::Cut] Cut196
  Base = -> Cut195
  Tool = -> Compound633
FEATURE [Part::Cylinder] Cylinder1258  label="Válec1258"
  Angle = 360
  AttacherType = Attacher::AttachEngine3D
  Height = 3
  Placement = pos=(26,41,-42) rot=(0,0,1;0rad)
  Radius = 3
FEATURE [Part::Cylinder] Cylinder1259  label="Válec1259"
  Angle = 360
  AttacherType = Attacher::AttachEngine3D
  Height = 3
  Placement = pos=(78,41,-42) rot=(0,0,1;0rad)
  Radius = 3
FEATURE [Part::Compound] Compound642
  Links = -> [Cylinder1258,Cylinder1259]
  Placement = pos=(-52,0,42) rot=(0,0,1;0rad)
FEATURE [Part::Cut] Cut197
  Base = -> Cut193
  Tool = -> Compound642
FEATURE [Part::Cut] Cut198
  Base = -> Cut196
  Tool = -> Compound627
FEATURE [Part::Cylinder] Cylinder1260  label="Válec1260"
  Angle = 360
  AttacherType = Attacher::AttachEngine3D
  Height = 100
  Placement = pos=(90,0,-60) rot=(0,0,1;0rad)
  Radius = 1.5
FEATURE [Part::Cylinder] Cylinder1261  label="Válec1261"
  Angle = 360
  AttacherType = Attacher::AttachEngine3D
  Height = 100
  Placement = pos=(14,0,-60) rot=(0,0,1;0rad)
  Radius = 1.5
FEATURE [Part::Compound] Compound644  label="srouby_troj003"
  Links = -> [Cylinder1260,Cylinder1261]
  Placement = pos=(-52,0,0) rot=(0,0,1;0rad)
FEATURE [Part::Cylinder] Cylinder1262  label="Válec1262"
  Angle = 360
  AttacherType = Attacher::AttachEngine3D
  Height = 32
  Placement = pos=(26,41,-42) rot=(0,0,1;0rad)
  Radius = 1.5
FEATURE [Part::Cylinder] Cylinder1263  label="Válec1263"
  Angle = 360
  AttacherType = Attacher::AttachEngine3D
  Height = 32
  Placement = pos=(78,41,-42) rot=(0,0,1;0rad)
  Radius = 1.5
FEATURE [Part::Compound] Compound645
  Links = -> [Cylinder1262,Cylinder1263]
  Placement = pos=(-52,0,36) rot=(0,0,1;0rad)
FEATURE [Part::Compound] Compound643
  Links = -> [Compound644,Compound645]
FEATURE [Part::Cut] Cut199
  Base = -> Cut173
  Tool = -> Compound643
FEATURE [Part::Box] Box238  label="Krychle238"
  AttacherType = Attacher::AttachEngine3D
  Height = 64
  Length = 6
  Placement = pos=(11,-3,-93) rot=(0,0,1;0rad)
  Width = 6
FEATURE [Part::Box] Box239  label="Krychle239"
  AttacherType = Attacher::AttachEngine3D
  Height = 64
  Length = 6
  Placement = pos=(87,-3,-93) rot=(0,0,1;0rad)
  Width = 6
FEATURE [Part::Compound] Compound646
  Links = -> [Box238,Box239]
  Placement = pos=(-52,0,36) rot=(0,0,1;0rad)
FEATURE [Part::Cut] Cut200
  Base = -> Cut199
  Tool = -> Compound646
FEATURE [Part::Cut] Cut201
  Base = -> Box142
  Tool = -> Compound628
FEATURE [Part::Cut] Cut202
  Base = -> Cut201
  Tool = -> Compound634
FEATURE [Part::Cut] Cut203
  Base = -> Cut202
  Tool = -> Compound630
FEATURE [Part::Cylinder] Cylinder1264  label="Válec1264"
  Angle = 360
  AttacherType = Attacher::AttachEngine3D
  Height = 100
  Placement = pos=(90,0,-60) rot=(0,0,1;0rad)
  Radius = 1.5
FEATURE [Part::Cylinder] Cylinder1265  label="Válec1265"
  Angle = 360
  AttacherType = Attacher::AttachEngine3D
  Height = 100
  Placement = pos=(14,0,-60) rot=(0,0,1;0rad)
  Radius = 1.5
FEATURE [Part::Compound] Compound648  label="srouby_troj004"
  Links = -> [Cylinder1264,Cylinder1265]
  Placement = pos=(-52,0,0) rot=(0,0,1;0rad)
FEATURE [Part::Cylinder] Cylinder1266  label="Válec1266"
  Angle = 360
  AttacherType = Attacher::AttachEngine3D
  Height = 32
  Placement = pos=(26,41,-42) rot=(0,0,1;0rad)
  Radius = 1.5
FEATURE [Part::Cylinder] Cylinder1267  label="Válec1267"
  Angle = 360
  AttacherType = Attacher::AttachEngine3D
  Height = 32
  Placement = pos=(78,41,-42) rot=(0,0,1;0rad)
  Radius = 1.5
FEATURE [Part::Compound] Compound649
  Links = -> [Cylinder1266,Cylinder1267]
  Placement = pos=(-52,0,36) rot=(0,0,1;0rad)
FEATURE [Part::Compound] Compound647
  Links = -> [Compound648,Compound649]
FEATURE [Part::Cut] Cut204
  Base = -> Cut197
  Tool = -> Compound647
FEATURE [Part::Cylinder] Cylinder490  label="Válec490"
  Angle = 360
  AttacherType = Attacher::AttachEngine3D
  Height = 10
  Radius = 60
FEATURE [Part::Cylinder] Cylinder491  label="Válec491"
  Angle = 360
  AttacherType = Attacher::AttachEngine3D
  Height = 10
  Radius = 52
FEATURE [Part::Cylinder] Cylinder492  label="Válec492"
  Angle = 360
  AttacherType = Attacher::AttachEngine3D
  Height = 20
  Placement = pos=(24,-40,-5) rot=(1,0,0;1.5708rad)
  Radius = 1.5
FEATURE [Part::Box] Box047  label="Krychle047"
  AttacherType = Attacher::AttachEngine3D
  Height = 6
  Length = 6
  Placement = pos=(-27,-47,-8) rot=(0,0,1;0rad)
  Width = 2
FEATURE [Part::Box] Box172  label="Krychle172"
  AttacherType = Attacher::AttachEngine3D
  Height = 6
  Length = 6
  Placement = pos=(48,-45,4) rot=(0,0,1;0rad)
  Width = 2
FEATURE [Part::Cylinder] Cylinder493  label="Válec493"
  Angle = 360
  AttacherType = Attacher::AttachEngine3D
  Height = 10
  Placement = pos=(0,0,20) rot=(0,0,1;0rad)
  Radius = 52
FEATURE [Part::Cylinder] Cylinder494  label="Válec494"
  Angle = 360
  AttacherType = Attacher::AttachEngine3D
  Height = 40
  Placement = pos=(59,-17,0) rot=(0,0,1;0rad)
  Radius = 10
FEATURE [Part::FeaturePython] wormgear027  # WARN: FeaturePython — macro-defined, semantics opaque (R4)
  AttacherType = Attacher::AttachEngine3D
  Placement = pos=(0,0,0) rot=(0,0,1;0.009355rad)
  beta = 29.4806
  clearance = 0.25
  diameter = 79.6
  head = 0
  height = 20
  module = 1
  pressure_angle = 20
  reverse_pitch = false
  teeth = 45
  version = 0.0.3
FEATURE [Part::Cut] Cut056
  Base = -> Cylinder491
  Tool = -> wormgear027
FEATURE [Part::FeaturePython] wormgear026  # WARN: FeaturePython — macro-defined, semantics opaque (R4)
  AttacherType = Attacher::AttachEngine3D
  beta = 29.4806
  clearance = 0.25
  diameter = 79.6
  head = 0
  height = 20
  module = 1
  pressure_angle = 20
  reverse_pitch = true
  teeth = 45
  version = 0.0.3
FEATURE [Part::Cut] Cut057
  Base = -> Cylinder490
  Placement = pos=(0,0,10) rot=(0,0,1;0.034907rad)
  Tool = -> wormgear026
FEATURE [Part::FeaturePython] Tube025  # WARN: FeaturePython — macro-defined, semantics opaque (R4)
  AttacherType = Attacher::AttachEngine3D
  Height = 8
  InnerRadius = 42
  OuterRadius = 52
  Placement = pos=(0,0,-8) rot=(0,0,1;0rad)
FEATURE [Part::Compound] Compound157
  Links = -> [Cut057,Cut056]
FEATURE [Part::Box] Box173  label="Krychle173"
  AttacherType = Attacher::AttachEngine3D
  Height = 6
  Length = 6
  Placement = pos=(21,-47,-8) rot=(0,0,1;0rad)
  Width = 2
FEATURE [Part::Box] Box045  label="Krychle045"
  AttacherType = Attacher::AttachEngine3D
  Height = 10
  Length = 108
  Placement = pos=(-54,-53,20) rot=(0,0,1;0rad)
  Width = 36
FEATURE [Part::Cut] Cut184
  Base = -> Box045
  Placement = pos=(0,0,-20) rot=(0,0,1;0rad)
  Tool = -> Cylinder493
FEATURE [Part::Cylinder] Cylinder495  label="Válec495"
  Angle = 360
  AttacherType = Attacher::AttachEngine3D
  Height = 40
  Placement = pos=(-59,-17,0) rot=(0,0,1;0rad)
  Radius = 10
FEATURE [Part::Compound] Compound163
  Links = -> [Cylinder494,Cylinder495]
FEATURE [Part::Cylinder] Cylinder496  label="Válec496"
  Angle = 360
  AttacherType = Attacher::AttachEngine3D
  Height = 8
  Placement = pos=(0,0,20) rot=(0,0,1;0rad)
  Radius = 52
FEATURE [Part::Box] Box174  label="Krychle174"
  AttacherType = Attacher::AttachEngine3D
  Height = 8
  Length = 108
  Placement = pos=(-54,-53,20) rot=(0,0,1;0rad)
  Width = 36
FEATURE [Part::Cut] Cut183
  Base = -> Box174
  Placement = pos=(0,0,-20) rot=(0,0,1;0rad)
  Tool = -> Cylinder496
FEATURE [Part::Cut] Cut185
  Base = -> Cut183
  Placement = pos=(0,0,-8) rot=(0,0,1;0rad)
  Tool = -> Compound163
FEATURE [Part::Cylinder] Cylinder497  label="Válec497"
  Angle = 360
  AttacherType = Attacher::AttachEngine3D
  Height = 40
  Placement = pos=(-59,-17,0) rot=(0,0,1;0rad)
  Radius = 10
FEATURE [Part::Box] Box046  label="Krychle046"
  AttacherType = Attacher::AttachEngine3D
  Height = 10
  Length = 108
  Placement = pos=(-54,-53,20) rot=(0,0,1;0rad)
  Width = 36
FEATURE [Part::Cylinder] Cylinder498  label="Válec498"
  Angle = 360
  AttacherType = Attacher::AttachEngine3D
  Height = 20
  Placement = pos=(-24,-40,-5) rot=(1,0,0;1.5708rad)
  Radius = 1.5
FEATURE [Part::Cylinder] Cylinder499  label="Válec499"
  Angle = 360
  AttacherType = Attacher::AttachEngine3D
  Height = 40
  Placement = pos=(59,-17,0) rot=(0,0,1;0rad)
  Radius = 10
FEATURE [Part::Compound] Compound162
  Links = -> [Cylinder499,Cylinder497]
FEATURE [Part::Cut] Cut188
  Base = -> Cut184
  Tool = -> Compound162
FEATURE [Part::Cylinder] Cylinder500  label="Válec500"
  Angle = 360
  AttacherType = Attacher::AttachEngine3D
  Height = 10
  Placement = pos=(0,0,20) rot=(0,0,1;0rad)
  Radius = 52
FEATURE [Part::Cut] Cut205
  Base = -> Box046
  Placement = pos=(0,0,-10) rot=(0,0,1;0rad)
  Tool = -> Cylinder500
FEATURE [Part::Cylinder] Cylinder501  label="Válec501"
  Angle = 360
  AttacherType = Attacher::AttachEngine3D
  Height = 20
  Placement = pos=(-51,-40,7) rot=(1,0,0;1.5708rad)
  Radius = 1.5
FEATURE [Part::Cylinder] Cylinder502  label="Válec502"
  Angle = 360
  AttacherType = Attacher::AttachEngine3D
  Height = 20
  Placement = pos=(-39.598,39.598,2) rot=(0,0,1;3.92699rad)
  Radius = 1.5
FEATURE [Part::Cylinder] Cylinder503  label="Válec503"
  Angle = 360
  AttacherType = Attacher::AttachEngine3D
  Height = 20
  Placement = pos=(-39.598,-39.598,2) rot=(0,0,-1;0.785398rad)
  Radius = 1.5
FEATURE [Part::Box] Box051  label="Krychle051"
  AttacherType = Attacher::AttachEngine3D
  Height = 6
  Length = 6
  Placement = pos=(-54,-45,4) rot=(0,0,1;0rad)
  Width = 2
FEATURE [Part::Compound] Compound169
  Links = -> [Box047,Box173,Box172,Box051]
FEATURE [Part::Cylinder] Cylinder504  label="Válec504"
  Angle = 360
  AttacherType = Attacher::AttachEngine3D
  Height = 20
  Placement = pos=(39.598,39.598,2) rot=(0,0,1;2.35619rad)
  Radius = 1.5
FEATURE [Part::Cylinder] Cylinder505  label="Válec505"
  Angle = 360
  AttacherType = Attacher::AttachEngine3D
  Height = 20
  Placement = pos=(56,0,2) rot=(0,0,1;1.5708rad)
  Radius = 1.5
FEATURE [Part::Cylinder] Cylinder154  label="Válec154"
  Angle = 360
  AttacherType = Attacher::AttachEngine3D
  Height = 20
  Placement = pos=(-1.2e-14,56,2) rot=(0,0,1;3.14159rad)
  Radius = 1.5
FEATURE [Part::Cylinder] Cylinder155  label="Válec155"
  Angle = 360
  AttacherType = Attacher::AttachEngine3D
  Height = 20
  Placement = pos=(0,-56,2) rot=(0,0,1;0rad)
  Radius = 1.5
FEATURE [Part::Cylinder] Cylinder506  label="Válec506"
  Angle = 360
  AttacherType = Attacher::AttachEngine3D
  Height = 20
  Placement = pos=(56,0,2) rot=(0,0,1;1.5708rad)
  Radius = 1.5
FEATURE [Part::Cylinder] Cylinder507  label="Válec507"
  Angle = 360
  AttacherType = Attacher::AttachEngine3D
  Height = 20
  Placement = pos=(51,-40,7) rot=(1,0,0;1.5708rad)
  Radius = 1.5
FEATURE [Part::Compound] Compound172
  Links = -> [Cylinder498,Cylinder492,Cylinder507,Cylinder501]
FEATURE [Part::Cylinder] Cylinder508  label="Válec508"
  Angle = 360
  AttacherType = Attacher::AttachEngine3D
  Height = 20
  Placement = pos=(0,-56,2) rot=(0,0,1;0rad)
  Radius = 1.5
FEATURE [Part::Cylinder] Cylinder509  label="Válec509"
  Angle = 360
  AttacherType = Attacher::AttachEngine3D
  Height = 20
  Placement = pos=(-56,-1.3e-14,2) rot=(0,0,-1;1.5708rad)
  Radius = 1.5
FEATURE [Part::Cylinder] Cylinder510  label="Válec510"
  Angle = 360
  AttacherType = Attacher::AttachEngine3D
  Height = 20
  Placement = pos=(-1.2e-14,56,2) rot=(0,0,1;3.14159rad)
  Radius = 1.5
FEATURE [Part::Cylinder] Cylinder511  label="Válec511"
  Angle = 360
  AttacherType = Attacher::AttachEngine3D
  Height = 20
  Placement = pos=(-39.598,39.598,2) rot=(0,0,1;3.92699rad)
  Radius = 1.5
FEATURE [Part::Cylinder] Cylinder512  label="Válec512"
  Angle = 360
  AttacherType = Attacher::AttachEngine3D
  Height = 20
  Placement = pos=(39.598,-39.598,2) rot=(0,0,1;0.785398rad)
  Radius = 1.5
FEATURE [Part::Cylinder] Cylinder513  label="Válec513"
  Angle = 360
  AttacherType = Attacher::AttachEngine3D
  Height = 20
  Placement = pos=(-39.598,-39.598,2) rot=(0,0,-1;0.785398rad)
  Radius = 1.5
FEATURE [Part::Compound] Compound164
  Links = -> [Cylinder508,Cylinder512,Cylinder506,Cylinder504,Cylinder510,Cylinder502,Cylinder509,Cylinder513]
FEATURE [Part::Cut] Cut187
  Base = -> Compound157
  Tool = -> Compound164
FEATURE [Part::Cylinder] Cylinder514  label="Válec514"
  Angle = 360
  AttacherType = Attacher::AttachEngine3D
  Height = 20
  Placement = pos=(-39.6,-39.6,-10) rot=(0,0,-1;0.785398rad)
  Radius = 4
FEATURE [Part::Box] Box057  label="Krychle057"
  AttacherType = Attacher::AttachEngine3D
  Height = 6
  Length = 6
  Placement = pos=(21,-47,-8) rot=(0,0,1;0rad)
  Width = 2
FEATURE [Part::Box] Box058  label="Krychle058"
  AttacherType = Attacher::AttachEngine3D
  Height = 6
  Length = 6
  Placement = pos=(-27,-47,-8) rot=(0,0,1;0rad)
  Width = 2
FEATURE [Part::Cylinder] Cylinder156  label="Válec156"
  Angle = 360
  AttacherType = Attacher::AttachEngine3D
  Height = 20
  Placement = pos=(39.598,39.598,2) rot=(0,0,1;2.35619rad)
  Radius = 1.5
FEATURE [Part::Cylinder] Cylinder515  label="Válec515"
  Angle = 360
  AttacherType = Attacher::AttachEngine3D
  Height = 20
  Placement = pos=(39.6,-39.6,-10) rot=(0,0,1;0.785398rad)
  Radius = 4
FEATURE [Part::Compound] Compound166
  Links = -> [Cylinder514,Cylinder515]
FEATURE [Part::Cut] Cut069
  Base = -> Cut187
  Tool = -> Compound166
FEATURE [Part::Cylinder] Cylinder164  label="Válec164"
  Angle = 360
  AttacherType = Attacher::AttachEngine3D
  Height = 20
  Placement = pos=(-39.6,-39.6,-10) rot=(0,0,-1;0.785398rad)
  Radius = 4
FEATURE [Part::Cylinder] Cylinder162  label="Válec162"
  Angle = 360
  AttacherType = Attacher::AttachEngine3D
  Height = 20
  Placement = pos=(-39.6,-39.6,-10) rot=(0,0,-1;0.785398rad)
  Radius = 4
FEATURE [Part::Cylinder] Cylinder163  label="Válec163"
  Angle = 360
  AttacherType = Attacher::AttachEngine3D
  Height = 20
  Placement = pos=(39.6,-39.6,-10) rot=(0,0,1;0.785398rad)
  Radius = 4
FEATURE [Part::Compound] Compound168
  Links = -> [Cylinder164,Cylinder163]
FEATURE [Part::Cut] Cut071
  Base = -> Cut188
  Tool = -> Compound168
FEATURE [Part::Box] Box052  label="Krychle052"
  AttacherType = Attacher::AttachEngine3D
  Height = 6
  Length = 6
  Placement = pos=(48,-45,4) rot=(0,0,1;0rad)
  Width = 2
FEATURE [Part::Box] Box053  label="Krychle053"
  AttacherType = Attacher::AttachEngine3D
  Height = 6
  Length = 6
  Placement = pos=(17,-47,-8) rot=(0,0,1;0rad)
  Width = 2
FEATURE [Part::Box] Box054  label="Krychle054"
  AttacherType = Attacher::AttachEngine3D
  Height = 6
  Length = 6
  Placement = pos=(-23,-47,-8) rot=(0,0,1;0rad)
  Width = 2
FEATURE [Part::Cylinder] Cylinder161  label="Válec161"
  Angle = 360
  AttacherType = Attacher::AttachEngine3D
  Height = 20
  Placement = pos=(39.6,-39.6,-10) rot=(0,0,1;0.785398rad)
  Radius = 4
FEATURE [Part::Compound] Compound167
  Links = -> [Cylinder162,Cylinder161]
FEATURE [Part::Cut] Cut070
  Base = -> Cut185
  Tool = -> Compound167
FEATURE [Part::Cut] Cut072
  Base = -> Cut070
  Tool = -> Compound169
FEATURE [Part::Box] Box055  label="Krychle055"
  AttacherType = Attacher::AttachEngine3D
  Height = 6
  Length = 6
  Placement = pos=(-54,-45,4) rot=(0,0,1;0rad)
  Width = 2
FEATURE [Part::Compound] Compound170
  Links = -> [Box054,Box053,Box052,Box055]
FEATURE [Part::Cut] Cut186
  Base = -> Cut071
  Tool = -> Compound170
FEATURE [Part::Box] Box056  label="Krychle056"
  AttacherType = Attacher::AttachEngine3D
  Height = 6
  Length = 6
  Placement = pos=(48,-45,4) rot=(0,0,1;0rad)
  Width = 2
FEATURE [Part::Cylinder] Cylinder516  label="Válec516"
  Angle = 360
  AttacherType = Attacher::AttachEngine3D
  Height = 20
  Placement = pos=(-56,-1.3e-14,2) rot=(0,0,-1;1.5708rad)
  Radius = 1.5
FEATURE [Part::Cylinder] Cylinder517  label="Válec517"
  Angle = 360
  AttacherType = Attacher::AttachEngine3D
  Height = 20
  Placement = pos=(39.598,-39.598,2) rot=(0,0,1;0.785398rad)
  Radius = 1.5
FEATURE [Part::Compound] Compound165
  Links = -> [Cylinder155,Cylinder517,Cylinder505,Cylinder156,Cylinder154,Cylinder511,Cylinder516,Cylinder503]
FEATURE [Part::Cut] Cut181
  Base = -> Cut205
  Tool = -> Compound165
FEATURE [Part::Box] Box062  label="Krychle062"
  AttacherType = Attacher::AttachEngine3D
  Height = 2
  Length = 6
  Placement = pos=(-41,-3,-4) rot=(0,0,1;1.5708rad)
  Width = 8
FEATURE [Part::Cylinder] Cylinder166  label="Válec166"
  Angle = 360
  AttacherType = Attacher::AttachEngine3D
  Height = 20
  Placement = pos=(24,-40,-5) rot=(1,0,0;1.5708rad)
  Radius = 1.5
FEATURE [Part::Cylinder] Cylinder167  label="Válec167"
  Angle = 360
  AttacherType = Attacher::AttachEngine3D
  Height = 20
  Placement = pos=(51,-40,7) rot=(1,0,0;1.5708rad)
  Radius = 1.5
FEATURE [Part::Box] Box061  label="Krychle061"
  AttacherType = Attacher::AttachEngine3D
  Height = 2
  Length = 6
  Placement = pos=(-31.1127,26.8701,-4) rot=(0,0,1;0.785398rad)
  Width = 8
FEATURE [Part::Box] Box067  label="Krychle067"
  AttacherType = Attacher::AttachEngine3D
  Height = 2
  Length = 6
  Placement = pos=(26.8701,31.1127,-4) rot=(0,0,-1;0.785398rad)
  Width = 8
FEATURE [Part::Cylinder] Cylinder175  label="Válec175"
  Angle = 360
  AttacherType = Attacher::AttachEngine3D
  Height = 20
  Placement = pos=(-45,-6e-15,-18) rot=(0,0,1;1.5708rad)
  Radius = 1.5
FEATURE [Part::Cylinder] Cylinder177  label="Válec177"
  Angle = 360
  AttacherType = Attacher::AttachEngine3D
  Height = 20
  Placement = pos=(1.4e-14,-45,-18) rot=(0,0,1;3.14159rad)
  Radius = 1.5
FEATURE [Part::Box] Box059  label="Krychle059"
  AttacherType = Attacher::AttachEngine3D
  Height = 6
  Length = 6
  Placement = pos=(-54,-45,4) rot=(0,0,1;0rad)
  Width = 2
FEATURE [Part::Compound] Compound171
  Links = -> [Box058,Box057,Box056,Box059]
FEATURE [Part::Cut] Cut182
  Base = -> Tube025
  Tool = -> Compound171
FEATURE [Part::Cut] Cut075
  Base = -> Cut182
  Tool = -> Compound172
FEATURE [Part::Cylinder] Cylinder170  label="Válec170"
  Angle = 360
  AttacherType = Attacher::AttachEngine3D
  Height = 20
  Placement = pos=(20,-40,-5) rot=(1,0,0;1.5708rad)
  Radius = 1.5
FEATURE [Part::Cylinder] Cylinder172  label="Válec172"
  Angle = 360
  AttacherType = Attacher::AttachEngine3D
  Height = 20
  Placement = pos=(-51,-40,7) rot=(1,0,0;1.5708rad)
  Radius = 1.5
FEATURE [Part::Cylinder] Cylinder169  label="Válec169"
  Angle = 360
  AttacherType = Attacher::AttachEngine3D
  Height = 20
  Placement = pos=(-20,-40,-5) rot=(1,0,0;1.5708rad)
  Radius = 1.5
FEATURE [Part::Cylinder] Cylinder168  label="Válec168"
  Angle = 360
  AttacherType = Attacher::AttachEngine3D
  Height = 20
  Placement = pos=(-51,-40,7) rot=(1,0,0;1.5708rad)
  Radius = 1.5
FEATURE [Part::Cylinder] Cylinder171  label="Válec171"
  Angle = 360
  AttacherType = Attacher::AttachEngine3D
  Height = 20
  Placement = pos=(51,-40,7) rot=(1,0,0;1.5708rad)
  Radius = 1.5
FEATURE [Part::Compound] Compound174
  Links = -> [Cylinder169,Cylinder170,Cylinder171,Cylinder172]
FEATURE [Part::Cut] Cut077
  Base = -> Cut186
  Tool = -> Compound174
FEATURE [Part::Box] Box060  label="Krychle060"
  AttacherType = Attacher::AttachEngine3D
  Height = 2
  Length = 6
  Placement = pos=(-3,41,-4) rot=(0,0,1;0rad)
  Width = 8
FEATURE [Part::Cylinder] Cylinder173  label="Válec173"
  Angle = 360
  AttacherType = Attacher::AttachEngine3D
  Height = 20
  Placement = pos=(0,45,-18) rot=(0,0,1;0rad)
  Radius = 1.5
FEATURE [Part::Cylinder] Cylinder165  label="Válec165"
  Angle = 360
  AttacherType = Attacher::AttachEngine3D
  Height = 20
  Placement = pos=(-24,-40,-5) rot=(1,0,0;1.5708rad)
  Radius = 1.5
FEATURE [Part::Compound] Compound173
  Links = -> [Cylinder165,Cylinder166,Cylinder167,Cylinder168]
FEATURE [Part::Cut] Cut076
  Base = -> Cut072
  Tool = -> Compound173
FEATURE [Part::Box] Box063  label="Krychle063"
  AttacherType = Attacher::AttachEngine3D
  Height = 2
  Length = 6
  Placement = pos=(-26.8701,-31.1127,-4) rot=(0,0,1;2.35619rad)
  Width = 8
FEATURE [Part::Box] Box064  label="Krychle064"
  AttacherType = Attacher::AttachEngine3D
  Height = 2
  Length = 6
  Placement = pos=(3,-41,-4) rot=(0,0,1;3.14159rad)
  Width = 8
FEATURE [Part::Box] Box065  label="Krychle065"
  AttacherType = Attacher::AttachEngine3D
  Height = 2
  Length = 6
  Placement = pos=(31.1127,-26.8701,-4) rot=(0,0,1;3.92699rad)
  Width = 8
FEATURE [Part::Box] Box066  label="Krychle066"
  AttacherType = Attacher::AttachEngine3D
  Height = 2
  Length = 6
  Placement = pos=(41,3,-4) rot=(0,0,-1;1.5708rad)
  Width = 8
FEATURE [Part::Compound] Compound175
  Links = -> [Box060,Box061,Box062,Box063,Box064,Box065,Box066,Box067]
  Placement = pos=(0,0,0) rot=(0,0,1;0.392699rad)
FEATURE [Part::Cut] Cut078
  Base = -> Cut075
  Tool = -> Compound175
FEATURE [Part::Cylinder] Cylinder174  label="Válec174"
  Angle = 360
  AttacherType = Attacher::AttachEngine3D
  Height = 20
  Placement = pos=(-31.8198,31.8198,-18) rot=(0,0,1;0.785398rad)
  Radius = 1.5
FEATURE [Part::Cylinder] Cylinder176  label="Válec176"
  Angle = 360
  AttacherType = Attacher::AttachEngine3D
  Height = 20
  Placement = pos=(-31.8198,-31.8198,-18) rot=(0,0,1;2.35619rad)
  Radius = 1.5
FEATURE [Part::Cylinder] Cylinder178  label="Válec178"
  Angle = 360
  AttacherType = Attacher::AttachEngine3D
  Height = 20
  Placement = pos=(31.8198,-31.8198,-18) rot=(0,0,1;3.92699rad)
  Radius = 1.5
FEATURE [Part::Cylinder] Cylinder179  label="Válec179"
  Angle = 360
  AttacherType = Attacher::AttachEngine3D
  Height = 20
  Placement = pos=(45,1.9e-14,-18) rot=(0,0,-1;1.5708rad)
  Radius = 1.5
FEATURE [Part::Cylinder] Cylinder180  label="Válec180"
  Angle = 360
  AttacherType = Attacher::AttachEngine3D
  Height = 20
  Placement = pos=(31.8198,31.8198,-18) rot=(0,0,-1;0.785398rad)
  Radius = 1.5
FEATURE [Part::Compound] Compound176
  Links = -> [Cylinder173,Cylinder174,Cylinder175,Cylinder176,Cylinder177,Cylinder178,Cylinder179,Cylinder180]
  Placement = pos=(0,0,0) rot=(0,0,1;0.392699rad)
FEATURE [Part::Cut] Cut079
  Base = -> Cut078
  Tool = -> Compound176
FEATURE [Part::Compound] Compound177  label="joint_max_monoblok1"
  Links = -> [Cut077,Cut079,Cut076,Cut069,Cut181]
FEATURE [Part::Fillet] Fillet004
  Base = -> Compound177
  Edges = 2 edges r=9: [Edge42,Edge278]
FEATURE [Part::Fillet] Fillet001  label="J-max_monoblok2"
  Base = -> Fillet004
  Edges = 2 edges r=8: [Edge30,Edge90]
FEATURE [Part::Box] Box108  label="Krychle108"
  AttacherType = Attacher::AttachEngine3D
  Height = 10
  Length = 10
  Placement = pos=(50,-43,10) rot=(0,0,1;0rad)
  Width = 43
FEATURE [Part::Cylinder] Cylinder518  label="Válec518"
  Angle = 360
  AttacherType = Attacher::AttachEngine3D
  Height = 20
  Placement = pos=(-39.598,-39.598,2) rot=(0,0,-1;0.785398rad)
  Radius = 1.5
FEATURE [Part::Cylinder] Cylinder519  label="Válec519"
  Angle = 360
  AttacherType = Attacher::AttachEngine3D
  Height = 20
  Placement = pos=(0,-56,2) rot=(0,0,1;0rad)
  Radius = 1.5
FEATURE [Part::Cylinder] Cylinder520  label="Válec520"
  Angle = 360
  AttacherType = Attacher::AttachEngine3D
  Height = 20
  Placement = pos=(-39.598,39.598,2) rot=(0,0,1;3.92699rad)
  Radius = 1.5
FEATURE [Part::Cylinder] Cylinder521  label="Válec521"
  Angle = 360
  AttacherType = Attacher::AttachEngine3D
  Height = 20
  Placement = pos=(56,0,2) rot=(0,0,1;1.5708rad)
  Radius = 1.5
FEATURE [Part::Cylinder] Cylinder522  label="Válec522"
  Angle = 360
  AttacherType = Attacher::AttachEngine3D
  Height = 10
  Placement = pos=(60,-43,10) rot=(0,0,1;0rad)
  Radius = 6
FEATURE [Part::Box] Box109  label="Krychle109"
  AttacherType = Attacher::AttachEngine3D
  Height = 10
  Length = 10
  Placement = pos=(-60,-43,10) rot=(0,0,1;0rad)
  Width = 43
FEATURE [Part::Compound] Compound239
  Links = -> [Box109,Box108]
FEATURE [Part::Cylinder] Cylinder523  label="Válec523"
  Angle = 360
  AttacherType = Attacher::AttachEngine3D
  Height = 20
  Placement = pos=(39.598,39.598,2) rot=(0,0,1;2.35619rad)
  Radius = 1.5
FEATURE [Part::Cylinder] Cylinder524  label="Válec524"
  Angle = 360
  AttacherType = Attacher::AttachEngine3D
  Height = 20
  Placement = pos=(39.598,-39.598,2) rot=(0,0,1;0.785398rad)
  Radius = 1.5
FEATURE [Part::Cylinder] Cylinder525  label="Válec525"
  Angle = 360
  AttacherType = Attacher::AttachEngine3D
  Height = 20
  Placement = pos=(-56,-1.3e-14,2) rot=(0,0,-1;1.5708rad)
  Radius = 1.5
FEATURE [Part::Cylinder] Cylinder526  label="Válec526"
  Angle = 360
  AttacherType = Attacher::AttachEngine3D
  Height = 10
  Placement = pos=(-60,-43,10) rot=(0,0,1;0rad)
  Radius = 6
FEATURE [Part::Compound] Compound241
  Links = -> [Cylinder522,Cylinder526]
FEATURE [Part::Cylinder] Cylinder527  label="Válec527"
  Angle = 360
  AttacherType = Attacher::AttachEngine3D
  Height = 20
  Placement = pos=(-1.2e-14,56,2) rot=(0,0,1;3.14159rad)
  Radius = 1.5
FEATURE [Part::Compound] Compound240
  Links = -> [Cylinder519,Cylinder524,Cylinder521,Cylinder523,Cylinder527,Cylinder520,Cylinder525,Cylinder518]
FEATURE [Part::Cut] Cut206
  Base = -> Compound239
  Tool = -> Compound240
FEATURE [Part::Cut] Cut207
  Base = -> Cut206
  Tool = -> Compound241
FEATURE [Part::Fillet] Fillet002
  Base = -> Cut207
  Edges = 2 edges r=4: [Edge4,Edge43]
FEATURE [Part::Compound] Compound242  label="J-max_monoblok"
  Links = -> [Fillet002,Fillet001]
  Placement = pos=(0,13,-53) rot=(0,0.707107,-0.707107;3.14159rad)
FEATURE [Part::Cylinder] Cylinder  label="Válec"
  Angle = 360
  AttacherType = Attacher::AttachEngine3D
  Height = 52
  Placement = pos=(0,13,-53) rot=(1,0,0;1.5708rad)
  Radius = 60.2
FEATURE [Part::Cut] Cut208
  Base = -> Cut203
  Tool = -> Cylinder
FEATURE [Part::Box] Box240  label="Krychle240"
  AttacherType = Attacher::AttachEngine3D
  Height = 64
  Length = 6
  Placement = pos=(11,-3,-93) rot=(0,0,1;0rad)
  Width = 6
FEATURE [Part::Box] Box241  label="Krychle241"
  AttacherType = Attacher::AttachEngine3D
  Height = 64
  Length = 6
  Placement = pos=(87,-3,-93) rot=(0,0,1;0rad)
  Width = 6
FEATURE [Part::Compound] Compound653
  Links = -> [Box240,Box241]
  Placement = pos=(-52,0,36) rot=(0,0,1;0rad)
FEATURE [Part::Cut] Cut209
  Base = -> Cut208
  Tool = -> Compound653
FEATURE [Part::Compound] Compound654  label="bazovina_part-A_triangle-support"
  Links = -> [Cut209,Cut190,Cut198,Cut200,Cut204]
FEATURE [Mesh::Feature] Mesh  label="bazovina_part-A_triangle-support (Meshed)"
